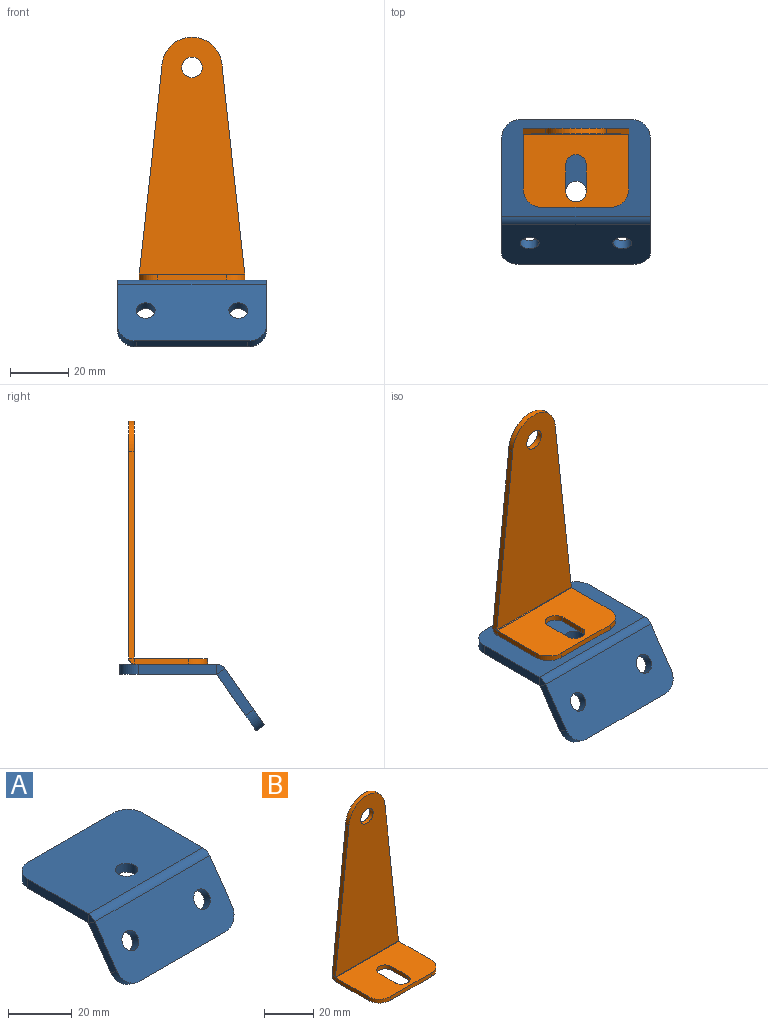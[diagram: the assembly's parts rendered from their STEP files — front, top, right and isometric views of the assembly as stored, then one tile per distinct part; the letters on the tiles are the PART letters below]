
ASSEMBLY  parts=2 mates=1
PART A: 21 faces, bbox 50.8x49.5x22.8 mm
  f0: plane 26.68x3.43mm, normal (1,0,0), area 91.5mm2, adj f4,f5,f6,f17
  f1: plane 26.68x3.43mm, normal (-1,0,0), area 91.5mm2, adj f4,f5,f7,f18
  f2: cylinder r=3.52mm len=7.04mm, axis (0,0,1), area 75.8mm2, adj f4,f5
  f3: plane 38.1x3.43mm, normal (0,1,0), area 130.6mm2, adj f4,f5,f6,f7
  f4: plane 50.8x33.03mm, normal (0,0,-1), area 1622mm2, adj f0,f1,f2,f3,f6,f7,f20
  f5: plane 50.8x33.03mm, normal (0,0,1), area 1622mm2, adj f0,f1,f2,f3,f6,f7,f19
  f6: cylinder r=6.35mm len=6.35mm, axis (0,0,-1), area 34.2mm2, adj f0,f3,f4,f5
  f7: cylinder r=6.35mm len=6.35mm, axis (0,0,-1), area 34.2mm2, adj f1,f3,f4,f5
  f8: plane 38.1x2.81mm, normal (0,-0.57,-0.82), area 130.6mm2, adj f13,f14,f15,f16
  f9: plane 16.02x12.65mm, normal (-1,0,0), area 58.8mm2, adj f13,f14,f15,f18
  f10: cylinder r=3.24mm len=7.27mm, axis (0,0.82,-0.57), area 69.8mm2, adj f13,f14
  f11: plane 16.02x12.65mm, normal (1,0,0), area 58.8mm2, adj f13,f14,f16,f17
  f12: cylinder r=3.24mm len=7.27mm, axis (0,0.82,-0.57), area 69.8mm2, adj f13,f14
  f13: plane 50.8x19.26mm, normal (0,0.82,-0.57), area 1111.1mm2, adj f8,f9,f10,f11,f12,f15,f16,f20
  f14: plane 50.8x19.26mm, normal (0,-0.82,0.57), area 1111.1mm2, adj f8,f9,f10,f11,f12,f15,f16,f19
  f15: cylinder r=6.35mm len=7.17mm, axis (0,0.82,-0.57), area 34.2mm2, adj f8,f9,f13,f14
  f16: cylinder r=6.35mm len=7.17mm, axis (0,0.82,-0.57), area 34.2mm2, adj f8,f11,f13,f14
  f17: plane 3.52x2.98mm, normal (1,0,0), area 6.3mm2, adj f0,f11,f19,f20
  f18: plane 3.52x2.98mm, normal (-1,0,0), area 6.3mm2, adj f1,f9,f19,f20
  f19: cylinder r=3.63mm len=50.8mm, axis (1,0,0), area 177.1mm2, adj f5,f14,f17,f18
  f20: cylinder r=0.2mm len=50.8mm, axis (1,0,0), area 9.9mm2, adj f4,f13,f17,f18
PART B: 21 faces, bbox 36.1x27x83.1 mm
  f0: plane 70.66x7.71mm, normal (-0.99,0,0.11), area 135.4mm2, adj f1,f4,f5,f18
  f1: cylinder r=10.31mm len=20.62mm, axis (0,-1,0), area 61.7mm2, adj f0,f3,f4,f5
  f2: cylinder r=3.52mm len=7.04mm, axis (0,-1,0), area 42.1mm2, adj f4,f5
  f3: plane 70.66x7.71mm, normal (0.99,0,0.11), area 135.4mm2, adj f1,f4,f5,f17
  f4: plane 80.98x36.04mm, normal (0,1,0), area 2130.2mm2, adj f0,f1,f2,f3,f19
  f5: plane 80.98x36.04mm, normal (0,-1,0), area 2130.2mm2, adj f0,f1,f2,f3,f20
  f6: plane 9.14x1.91mm, normal (1,0,0), area 17.4mm2, adj f7,f12,f13,f14
  f7: cylinder r=3.52mm len=7.04mm, axis (0,0,-1), area 21.1mm2, adj f6,f8,f13,f14
  f8: plane 9.14x1.91mm, normal (-1,0,0), area 17.4mm2, adj f7,f12,f13,f14
  f9: plane 23.38x1.91mm, normal (0,-1,0), area 44.5mm2, adj f13,f14,f15,f16
  f10: plane 18.53x1.91mm, normal (-1,0,0), area 35.3mm2, adj f13,f14,f15,f18
  f11: plane 18.53x1.91mm, normal (1,0,0), area 35.3mm2, adj f13,f14,f16,f17
  f12: cylinder r=3.52mm len=7.04mm, axis (0,0,-1), area 21.1mm2, adj f6,f8,f13,f14
  f13: plane 36.08x24.88mm, normal (0,0,-1), area 777.2mm2, adj f6,f7,f8,f9,f10,f11,f12,f15
  f14: plane 36.08x24.88mm, normal (0,0,1), area 777.2mm2, adj f6,f7,f8,f9,f10,f11,f12,f15
  f15: cylinder r=6.35mm len=6.35mm, axis (0,0,-1), area 19mm2, adj f9,f10,f13,f14
  f16: cylinder r=6.35mm len=6.35mm, axis (0,0,-1), area 19mm2, adj f9,f11,f13,f14
  f17: bspline ~2.11x2.11mm, area 3.5mm2, adj f3,f11,f19,f20
  f18: bspline ~2.11x2.11mm, area 3.5mm2, adj f0,f10,f19,f20
  f19: cylinder r=2.11mm len=36.08mm, axis (1,0,0), area 119.4mm2, adj f4,f13,f17,f18
  f20: cylinder r=0.2mm len=36.08mm, axis (1,0,0), area 11.5mm2, adj f5,f14,f17,f18
PLACE A t=(12.14,53.95,-118)mm
PLACE B t=(12.14,85.81,-114.57)mm
MATE revolute A.f2 <-> B.f7  axis (0,0,1) through (12.14,64.27,-114.57)mm
